# Revit family: Betonafstandsklods uden wire 45-55-60
name_source: partatom
category: Generic Models
units: mm (PartAtom-declared; Revit-internal decimal feet)

## family parameters
Always vertical = No
Can host rebar = No
Cut with Voids When Loaded = No
Part Type = Normal
Room Calculation Point = No
Round Connector Dimension = Use Diameter
Shared = No
Work Plane-Based = Yes

## types (1)
- Betonafstandsklods uden wire 45-55-60
    Bottom Curve = 50 mm  [stored 0.164042 ft]
    Default Elevation = 1219 mm
    Height = 60 mm  [stored 0.19685 ft]
    Numbers = Wall Texture, Orange Peel
    Side Curve = 50 mm  [stored 0.164042 ft]
    Side Curve R = 55 mm  [stored 0.180446 ft]
    Technical Data Sheet = https://haucon.dk
    Thickness = 30 mm  [stored 0.0984252 ft]
    Top Curve = 2 mm  [stored 0.00656168 ft]
    Top Curve R = 17 mm
    Website Link = https://haucon.dk
    Width = 65 mm  [stored 0.213255 ft]
    concrete = Concrete, C50/60

note: [stored X ft] marks values corroborated as IEEE doubles in the binary element streams (Revit-internal decimal feet)

## geometry (parser evidence)
native form markers: Sweep x2
no freeform markers — native parametric forms only
